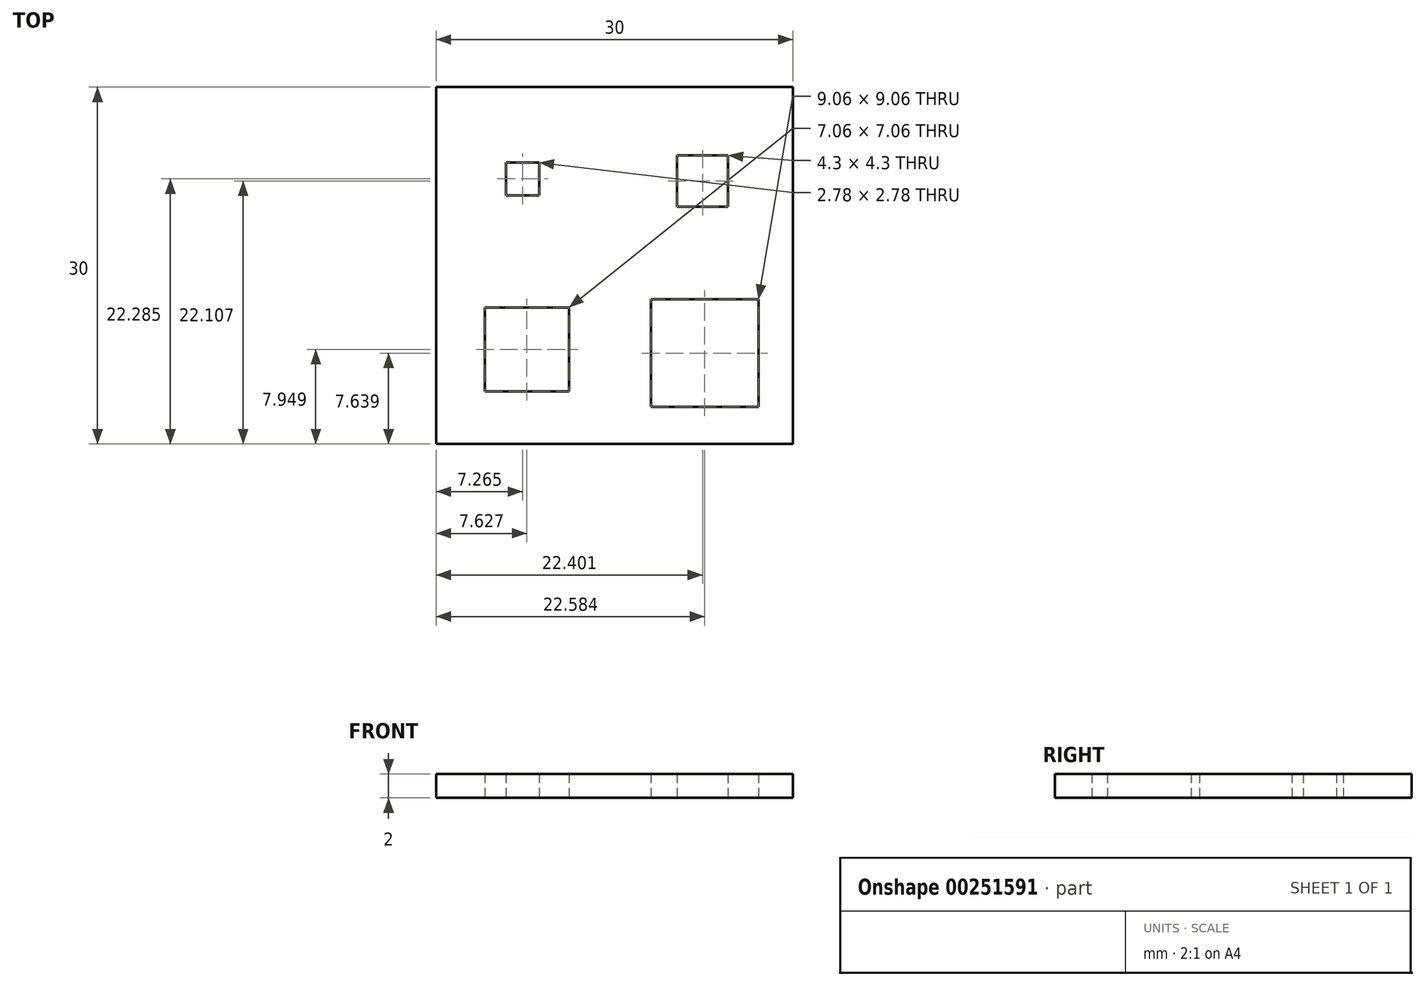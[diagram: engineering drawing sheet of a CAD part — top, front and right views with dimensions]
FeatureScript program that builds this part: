
annotation { "Feature Type Name" : "Feature", "Feature Type Description" : "" }
export const myFeature = defineFeature(function(context is Context, id is Id, definition is map)
    precondition{}
    {
        {
            var Q0;
            Q0=qCreatedBy(makeId("Top.planeOp"),FACE);
            var sketch = newSketch(context, id + "F0", { "sketchPlane" : qUnion([Q0])});
            skLineSegment(sketch, "E0.bottom", {"start": v(15, -15) * mm, "end": v(-15, -15) * mm});
            skLineSegment(sketch, "E0.top", {"start": v(15, 15) * mm, "end": v(-15, 15) * mm});
            skLineSegment(sketch, "E0.left", {"start": v(15, -15) * mm, "end": v(15, 15) * mm});
            skLineSegment(sketch, "E0.right", {"start": v(-15, -15) * mm, "end": v(-15, 15) * mm});
            skPoint(sketch, "E0.middle", {"position": v(0, 0) * mm});
            skLineSegment(sketch, "E1.bottom", {"start": v(-6.35, 5.9) * mm, "end": v(-9.13, 5.9) * mm});
            skLineSegment(sketch, "E1.top", {"start": v(-6.35, 8.68) * mm, "end": v(-9.13, 8.68) * mm});
            skLineSegment(sketch, "E1.left", {"start": v(-6.35, 5.9) * mm, "end": v(-6.35, 8.68) * mm});
            skLineSegment(sketch, "E1.right", {"start": v(-9.13, 5.9) * mm, "end": v(-9.13, 8.68) * mm});
            skPoint(sketch, "E1.middle", {"position": v(-7.74, 7.29) * mm});
            skLineSegment(sketch, "E2.bottom", {"start": v(9.55, 4.96) * mm, "end": v(5.25, 4.96) * mm});
            skLineSegment(sketch, "E2.top", {"start": v(9.55, 9.26) * mm, "end": v(5.25, 9.26) * mm});
            skLineSegment(sketch, "E2.left", {"start": v(9.55, 4.96) * mm, "end": v(9.55, 9.26) * mm});
            skLineSegment(sketch, "E2.right", {"start": v(5.25, 4.96) * mm, "end": v(5.25, 9.26) * mm});
            skPoint(sketch, "E2.middle", {"position": v(7.4, 7.1) * mm});
            skLineSegment(sketch, "E3.bottom", {"start": v(-3.84, -10.58) * mm, "end": v(-10.9, -10.58) * mm});
            skLineSegment(sketch, "E3.top", {"start": v(-3.84, -3.52) * mm, "end": v(-10.9, -3.52) * mm});
            skLineSegment(sketch, "E3.left", {"start": v(-3.84, -10.58) * mm, "end": v(-3.84, -3.52) * mm});
            skLineSegment(sketch, "E3.right", {"start": v(-10.9, -10.58) * mm, "end": v(-10.9, -3.52) * mm});
            skPoint(sketch, "E3.middle", {"position": v(-7.37, -7.05) * mm});
            skLineSegment(sketch, "E4.bottom", {"start": v(12.11, -11.9) * mm, "end": v(3.05, -11.9) * mm});
            skLineSegment(sketch, "E4.top", {"start": v(12.11, -2.83) * mm, "end": v(3.05, -2.83) * mm});
            skLineSegment(sketch, "E4.left", {"start": v(12.11, -11.9) * mm, "end": v(12.11, -2.83) * mm});
            skLineSegment(sketch, "E4.right", {"start": v(3.05, -11.9) * mm, "end": v(3.05, -2.83) * mm});
            skPoint(sketch, "E4.middle", {"position": v(7.58, -7.36) * mm});
            skSolve(sketch);
        }
        {
            var Q0;
            Q0=makeQuery(id+"F0.imprint","IMPRINT",FACE,{"disambiguationData":[TD([[makeQuery(id+"F0.imprint","IMPRINT",EDGE,{"derivedFrom":sQuery(id+"F0.wireOp",EDGE,"E0.bottom")}),-1.0]])]});
            extrude(context, id + "F1", {"entities" : qUnion([Q0]), "depth" : 2 * mm});
        }
    });
